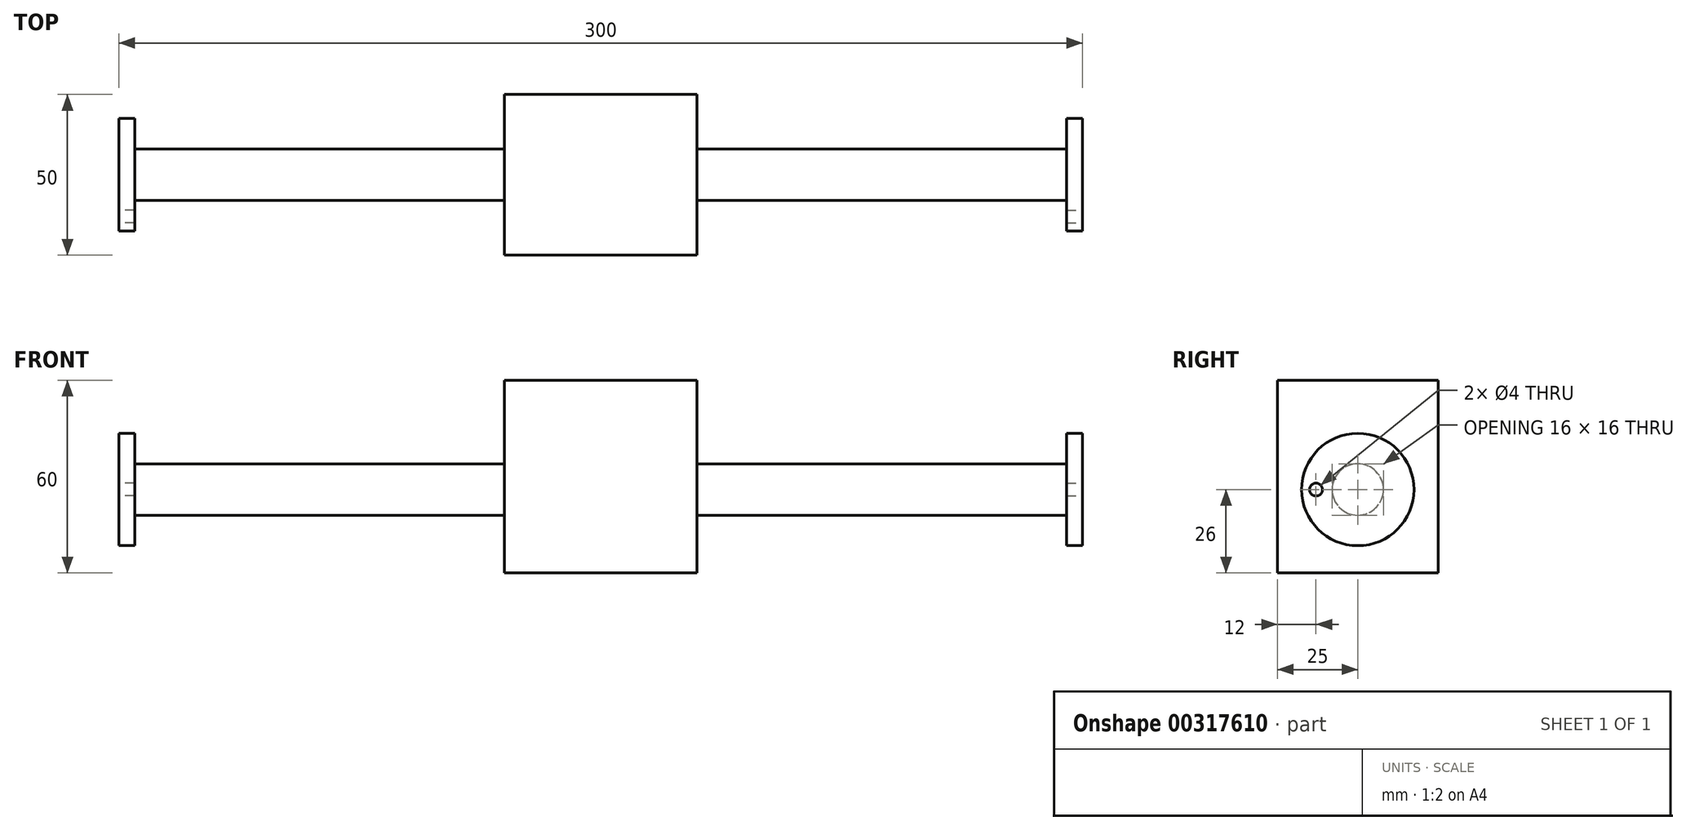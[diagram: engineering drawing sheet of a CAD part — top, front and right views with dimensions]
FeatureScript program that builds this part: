
annotation { "Feature Type Name" : "Feature", "Feature Type Description" : "" }
export const myFeature = defineFeature(function(context is Context, id is Id, definition is map)
    precondition{}
    {
        {
            var Q0;
            Q0=qCreatedBy(makeId("Right.planeOp"),FACE);
            cPlane(context, id + "F0", {"entities" : qUnion([Q0]), "cplaneType" : CPlaneType.OFFSET, "offset" : 150 * mm, "width" : 150 * mm, "height" : 150 * mm});
        }
        {
            var Q0;
            Q0=qCreatedBy(id+"F0.planeOp",FACE);
            var sketch = newSketch(context, id + "F1", { "sketchPlane" : qUnion([Q0])});
            skCircle(sketch, "E0", {"center": v(0, 0) * mm, "radius": 17.5 * mm});
            skSolve(sketch);
        }
        {
            var Q0;
            Q0=makeQuery(id+"F1.imprint","IMPRINT",FACE,{"disambiguationData":[TD([[makeQuery(id+"F1.imprint","IMPRINT",EDGE,{"derivedFrom":sQuery(id+"F1.wireOp",EDGE,"E0")}),1.0]])]});
            extrude(context, id + "F2", {"entities" : qUnion([Q0]), "oppositeDirection" : true, "depth" : 5 * mm});
        }
        {
            var Q0;
            Q0=qCreatedBy(makeId("Right.planeOp"),FACE);
            var sketch = newSketch(context, id + "F3", { "sketchPlane" : qUnion([Q0])});
            skLineSegment(sketch, "E1.bottom", {"start": v(25, 34) * mm, "end": v(-25, 34) * mm});
            skLineSegment(sketch, "E1.top", {"start": v(25, -26) * mm, "end": v(-25, -26) * mm});
            skLineSegment(sketch, "E1.left", {"start": v(25, 34) * mm, "end": v(25, -26) * mm});
            skLineSegment(sketch, "E1.right", {"start": v(-25, 34) * mm, "end": v(-25, -26) * mm});
            skSolve(sketch);
        }
        {
            var Q0;
            Q0=makeQuery(id+"F3.imprint","IMPRINT",FACE,{"disambiguationData":[TD([[makeQuery(id+"F3.imprint","IMPRINT",EDGE,{"derivedFrom":sQuery(id+"F3.wireOp",EDGE,"E1.bottom")}),1.0]])]});
            extrude(context, id + "F4", {"entities" : qUnion([Q0]), "depth" : 30 * mm});
        }
        {
            var Q0;
            Q0=makeQuery(id+"F2.opExtrude","CAP_FACE",FACE,{"disambiguationData":[OSD([sQuery(id+"F1.wireOp",EDGE,"E0")])],"isStart":false});
            var sketch = newSketch(context, id + "F5", { "sketchPlane" : qUnion([Q0])});
            skCircle(sketch, "E2", {"center": v(0, 0) * mm, "radius": 8 * mm});
            skSolve(sketch);
        }
        {
            var Q0;
            Q0=makeQuery(id+"F5.imprint","IMPRINT",FACE,{"disambiguationData":[TD([[makeQuery(id+"F5.imprint","IMPRINT",EDGE,{"derivedFrom":sQuery(id+"F5.wireOp",EDGE,"E2")}),1.0]])]});
            extrude(context, id + "F6", {"entities" : qUnion([Q0]), "endBound" : BoundingType.UP_TO_NEXT, "depth" : 25 * mm});
        }
        {
            var Q0;
            Q0=makeQuery(id+"F2.opExtrude","CAP_FACE",FACE,{"disambiguationData":[OSD([sQuery(id+"F1.wireOp",EDGE,"E0")])],"isStart":true});
            var sketch = newSketch(context, id + "F7", { "sketchPlane" : qUnion([Q0])});
            skCircle(sketch, "E3", {"center": v(-13, 0) * mm, "radius": 2 * mm});
            skSolve(sketch);
        }
        {
            var Q0;
            Q0=makeQuery(id+"F7.imprint","IMPRINT",FACE,{"disambiguationData":[TD([[makeQuery(id+"F7.imprint","IMPRINT",EDGE,{"derivedFrom":sQuery(id+"F7.wireOp",EDGE,"E3")}),1.0]])]});
            extrude(context, id + "F8", {"entities" : qUnion([Q0]), "operationType" : NewBodyOperationType.REMOVE, "oppositeDirection" : true, "depth" : 25 * mm});
        }
        {
            var Q0;
            Q0=makeQuery(id+"F4.opExtrude","SWEPT_BODY",BODY,{"disambiguationData":[OSD([sQuery(id+"F3.wireOp",EDGE,"E1.bottom"),sQuery(id+"F3.wireOp",EDGE,"E1.top"),sQuery(id+"F3.wireOp",EDGE,"E1.left"),sQuery(id+"F3.wireOp",EDGE,"E1.right")])]});
            var Q1;
            Q1=qCreatedBy(makeId("Right.planeOp"),FACE);
            mirror(context, id + "F9", {"operationType" : NewBodyOperationType.ADD, "entities" : qUnion([Q0]), "mirrorPlane" : qUnion([Q1])});
        }
        {
            var Q0;
            Q0=makeQuery(id+"F6.opExtrude","SWEPT_BODY",BODY,{"disambiguationData":[OSD([sQuery(id+"F5.wireOp",EDGE,"E2")])]});
            var Q1;
            Q1=qCreatedBy(makeId("Right.planeOp"),FACE);
            mirror(context, id + "F10", {"operationType" : NewBodyOperationType.ADD, "entities" : qUnion([Q0]), "mirrorPlane" : qUnion([Q1])});
        }
        {
            var Q0;
            Q0=makeQuery(id+"F2.opExtrude","SWEPT_BODY",BODY,{"disambiguationData":[OSD([sQuery(id+"F1.wireOp",EDGE,"E0")])]});
            var Q1;
            Q1=qCreatedBy(makeId("Right.planeOp"),FACE);
            mirror(context, id + "F11", {"operationType" : NewBodyOperationType.ADD, "entities" : qUnion([Q0]), "mirrorPlane" : qUnion([Q1])});
        }
    });
